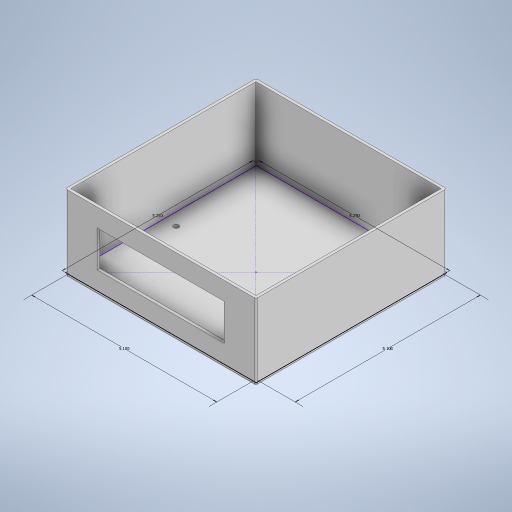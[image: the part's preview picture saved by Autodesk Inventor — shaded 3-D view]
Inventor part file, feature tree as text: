
AUTODESK INVENTOR PART (.ipt)
format: ipt  version: 2024.1 (Build 281209000, 209)  size: 287,744 bytes
history: native  units: in
note: dims shown in document units (in); Inventor stores cm internally (conversion verified against a paired STEP export)
features: sketch x3, extrude x3, fillet x1, hole x1, projected_geometry x1
ambient origin geometry x8: Origin, YZ Plane, XZ Plane, XY Plane, X Axis, Y Axis, Z Axis, Center Point
bodies: Solid1 (feature_tree)
feature tree (9):
  sketch  "Sketch1"  dims[d0=5.25in d1=5.25in]
  extrude  "Extrusion1"  Depth=5.25in
  extrude  "Extrusion2"  Depth=5.1in
  fillet  "Fillet1"  Radius=2.0in
  hole  "Hole1"  [1 undecoded]
  extrude  "Extrusion3"  Depth=0.1in
  sketch  "Sketch2"  dims[d2=5.1in d3=5.1in d4=2.0in d5=0.0in]
  projected_geometry  "Projected Loop1"
  sketch  "Sketch3"  dims[d6=0.1in d7=0.0in d8=0.05in d9=2.2in d10=0.0in d11=4.4in d12=0.144in d13=1.0in d14=0.375in d15=0.25in d16=0.5635in d17=1.0in d18=0.8108in d19=0.5in d20=1.75in d21=3.5in d22=1.0in d23=0.1in d24=0.0in]
note: 1 required parameter value undecoded (feature->parameter linkage not recoverable at this tier; creation-order binding heuristic only, values carry confidence <= 0.55)
